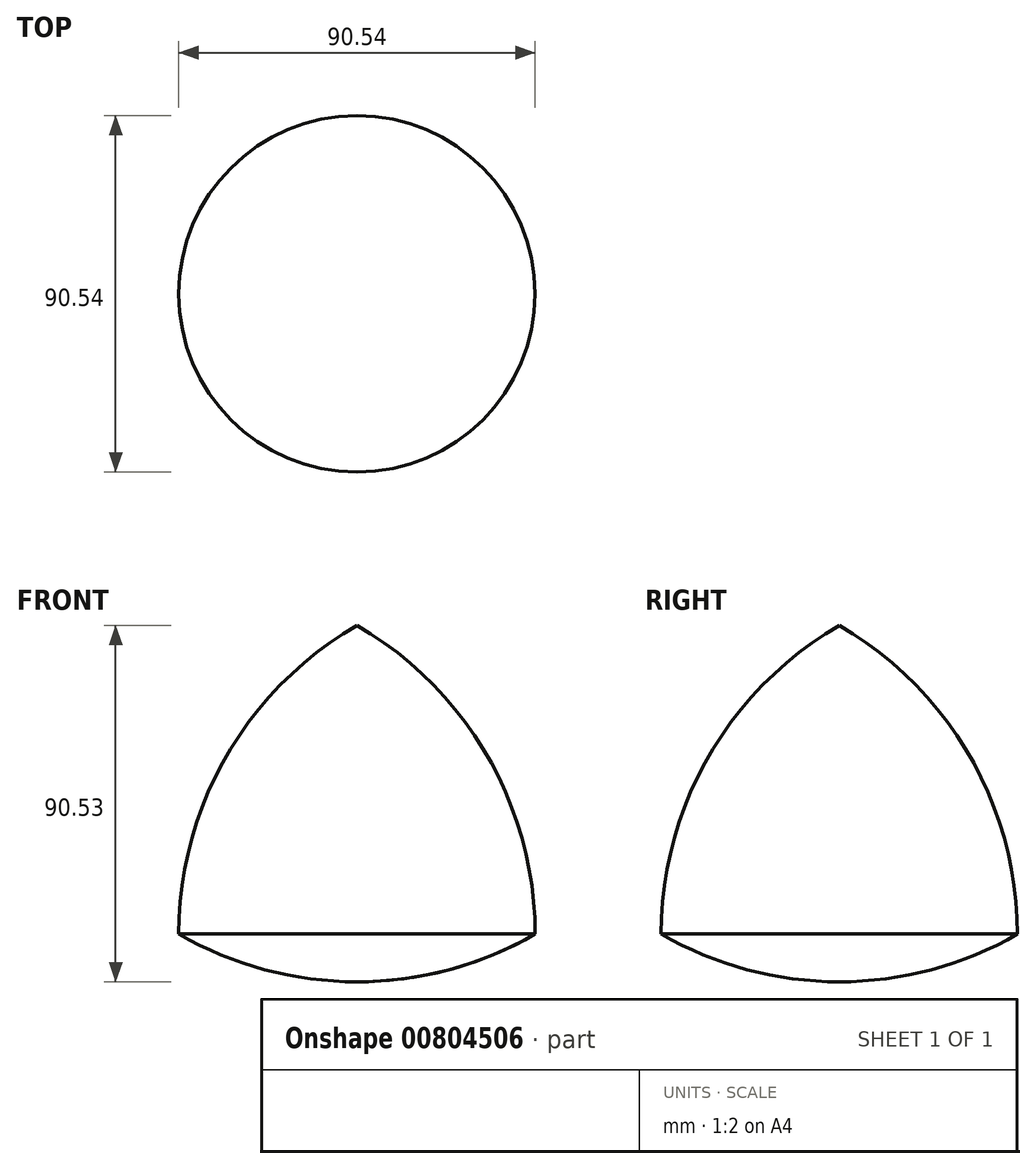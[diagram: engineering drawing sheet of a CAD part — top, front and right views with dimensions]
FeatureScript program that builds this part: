
annotation { "Feature Type Name" : "Feature", "Feature Type Description" : "" }
export const myFeature = defineFeature(function(context is Context, id is Id, definition is map)
    precondition{}
    {
        {
            var Q0;
            Q0=qCreatedBy(makeId("Front.planeOp"),FACE);
            var sketch = newSketch(context, id + "F0", { "sketchPlane" : qUnion([Q0])});
            skCircle(sketch, "E0.cCircle", {"center": v(0, 0) * mm, "radius": 26.13 * mm, "construction": true});
            skLineSegment(sketch, "E0.0", {"start": v(45.27, -26.13) * mm, "end": v(-45.27, -26.13) * mm});
            skLineSegment(sketch, "E0.1", {"start": v(-45.27, -26.13) * mm, "end": v(0, 52.27) * mm});
            skLineSegment(sketch, "E0.2", {"start": v(0, 52.27) * mm, "end": v(45.27, -26.13) * mm});
            skPoint(sketch, "E0.0.midPoint", {"position": v(0, -26.13) * mm});
            skLineSegment(sketch, "E1", {"start": v(0, 52.27) * mm, "end": v(0, -32.85) * mm});
            skCircle(sketch, "E2", {"center": v(-45.27, -26.13) * mm, "radius": 90.53 * mm});
            skCircle(sketch, "E3", {"center": v(0, 52.27) * mm, "radius": 90.53 * mm});
            skCircle(sketch, "E4", {"center": v(45.27, -26.13) * mm, "radius": 90.53 * mm});
            skLineSegment(sketch, "E5", {"start": v(0, 52.27) * mm, "end": v(0, -44.53) * mm});
            skSolve(sketch);
        }
        {
            var Q0;
            {var subQ4=sQuery(id+"F0.wireOp",EDGE,"E0.2");Q0=makeQuery(id+"F0.imprint","IMPRINT",FACE,{"disambiguationData":[TD([[makeQuery(id+"F0.imprint","IMPRINT",EDGE,{"derivedFrom":subQ4}),-1.0]])]});}
            var Q1;
            {var subQ0=sQuery(id+"F0.wireOp",EDGE,"E0.2");Q1=makeQuery(id+"F0.imprint","IMPRINT",FACE,{"disambiguationData":[TD([[makeQuery(id+"F0.imprint","IMPRINT",EDGE,{"derivedFrom":subQ0}),1.0]])]});}
            var Q2;
            {var subQ0=sQuery(id+"F0.wireOp",EDGE,"E1");var subQ1=sQuery(id+"F0.wireOp",EDGE,"E0.0");var subQ2=makeQuery(id+"F0.imprint","INTERSECT",VERTEX,{"derivedFrom":[subQ1,subQ0]});Q2=makeQuery(id+"F0.imprint","IMPRINT",FACE,{"disambiguationData":[TD([[makeQuery(id+"F0.imprint","IMPRINT",EDGE,{"disambiguationData":[TD([[subQ2,-1.0]])],"derivedFrom":subQ0}),1.0]])]});}
            var Q3;
            Q3=sQuery(id+"F0.wireOp",EDGE,"E5");
            revolve(context, id + "F1", {"surfaceOperationType" : NewSurfaceOperationType.NEW, "entities" : qUnion([Q0, Q1, Q2]), "axis" : qUnion([Q3]), "revolveType" : RevolveType.FULL});
        }
    });
